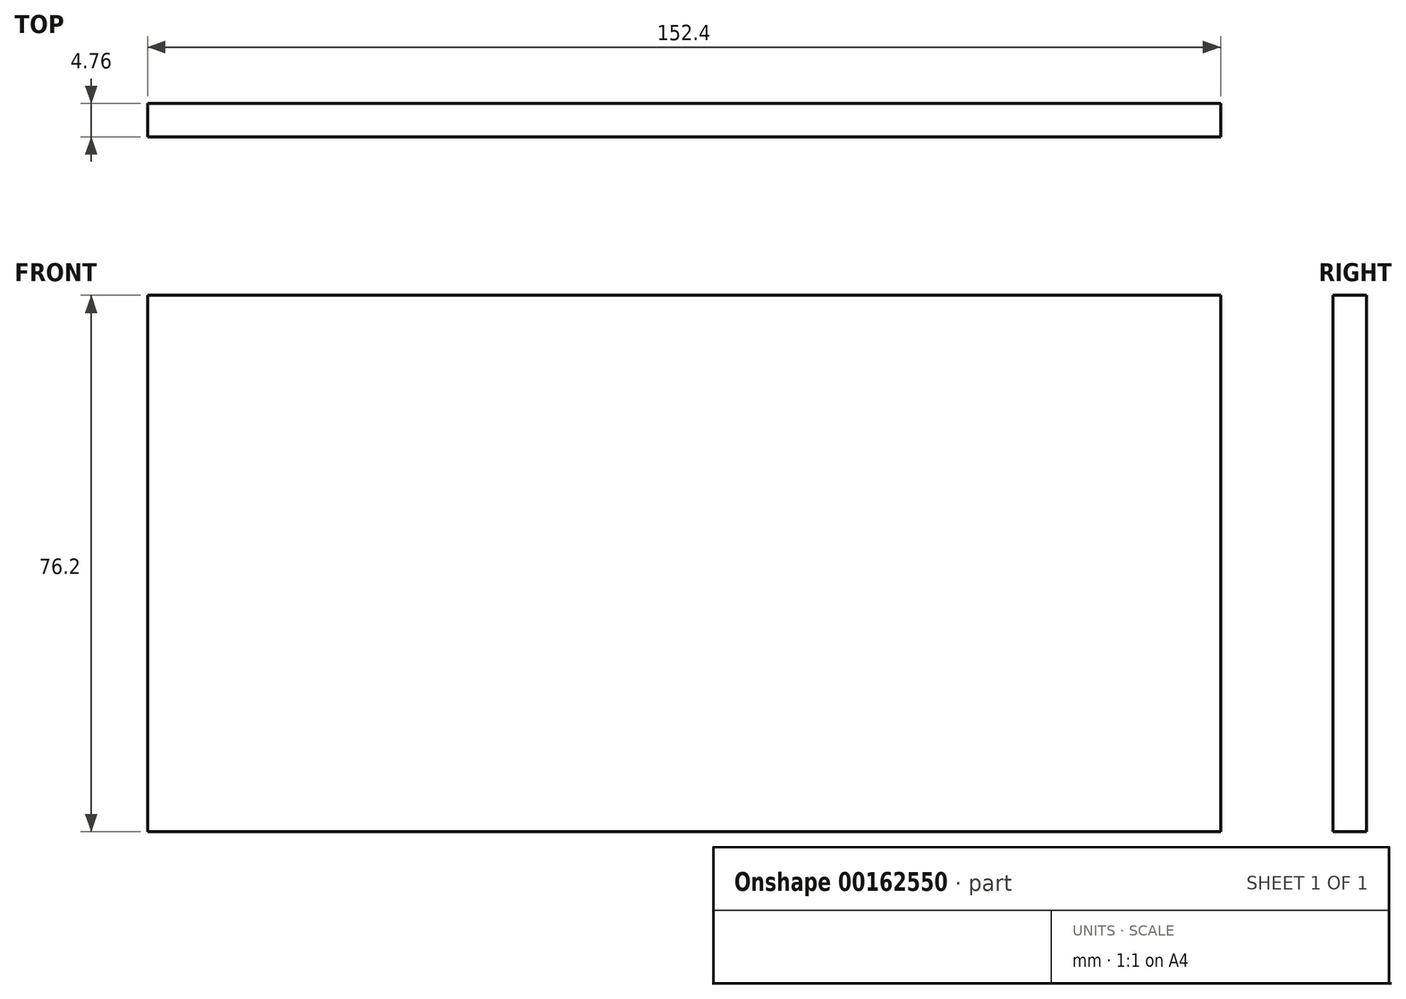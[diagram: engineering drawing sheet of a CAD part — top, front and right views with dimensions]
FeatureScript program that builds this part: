
annotation { "Feature Type Name" : "Feature", "Feature Type Description" : "" }
export const myFeature = defineFeature(function(context is Context, id is Id, definition is map)
    precondition{}
    {
        {
            var Q0;
            Q0=qCreatedBy(makeId("Front.planeOp"),FACE);
            var sketch = newSketch(context, id + "F0", { "sketchPlane" : qUnion([Q0])});
            skLineSegment(sketch, "E0.bottom", {"start": v(76.2, 38.1) * mm, "end": v(-76.2, 38.1) * mm});
            skLineSegment(sketch, "E0.top", {"start": v(76.2, -38.1) * mm, "end": v(-76.2, -38.1) * mm});
            skLineSegment(sketch, "E0.left", {"start": v(76.2, 38.1) * mm, "end": v(76.2, -38.1) * mm});
            skLineSegment(sketch, "E0.right", {"start": v(-76.2, 38.1) * mm, "end": v(-76.2, -38.1) * mm});
            skPoint(sketch, "E0.middle", {"position": v(0, 0) * mm});
            skSolve(sketch);
        }
        {
            var Q0;
            Q0=qSketchRegion(id+"F0",true);
            extrude(context, id + "F1", {"entities" : qUnion([Q0]), "depth" : 4.76 * mm});
        }
    });
